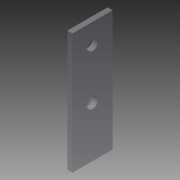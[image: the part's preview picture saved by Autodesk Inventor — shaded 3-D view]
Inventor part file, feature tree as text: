
AUTODESK INVENTOR PART (.ipt)
format: ipt  version: 2013 (Build 170138000, 138)  size: 77,312 bytes
history: native  units: in
note: dims shown in document units (in); Inventor stores cm internally (conversion verified against a paired STEP export)
features: extrude x1, sketch x1
ambient origin geometry x8: Origin, YZ Plane, XZ Plane, XY Plane, X Axis, Y Axis, Z Axis, Center Point
bodies: Solid1 (feature_tree)
feature tree (2):
  extrude  "Extrusion1"  Depth=1.0in
  sketch  "Sketch1"  dims[d0=3.0in d2=1.0in d3=0.26in d4=0.5in d5=1.25in d6=0.125in d7=0.0in]
